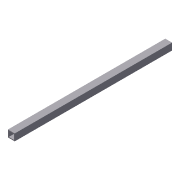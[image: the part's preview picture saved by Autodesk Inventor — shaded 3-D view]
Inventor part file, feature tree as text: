
AUTODESK INVENTOR PART (.ipt)
format: ipt  version: 2012 (Build 160160000, 160)  size: 71,168 bytes
history: native  units: in
note: dims shown in document units (in); Inventor stores cm internally (conversion verified against a paired STEP export)
features: extrude x1, shell x1, sketch x1
ambient origin geometry x8: Origin, YZ Plane, XZ Plane, XY Plane, X Axis, Y Axis, Z Axis, Center Point
bodies: Solid1 (feature_tree)
feature tree (3):
  extrude  "Extrusion1"  Depth=1.0in
  shell  "Shell1"  Thickness=23.0in
  sketch  "Sketch1"  dims[d0=1.0in d1=1.0in d2=23.0in d3=0.0in d4=0.125in]
